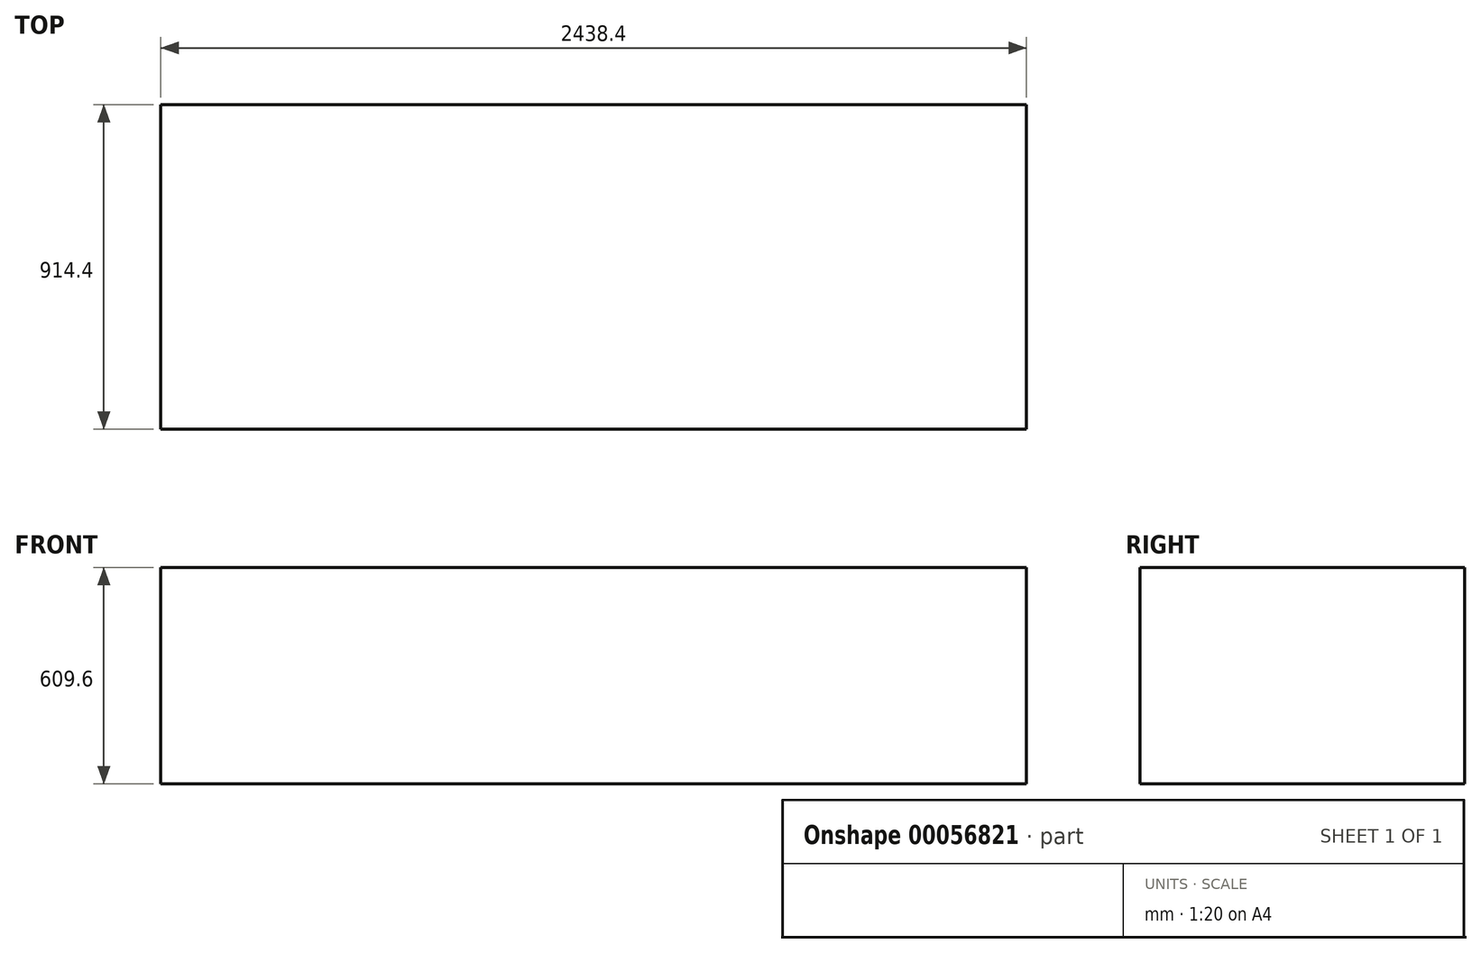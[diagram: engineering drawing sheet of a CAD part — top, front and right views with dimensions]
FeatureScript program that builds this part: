
annotation { "Feature Type Name" : "Feature", "Feature Type Description" : "" }
export const myFeature = defineFeature(function(context is Context, id is Id, definition is map)
    precondition{}
    {
        {
            var Q0;
            Q0=qCreatedBy(makeId("Top.planeOp"),FACE);
            var sketch = newSketch(context, id + "F0", { "sketchPlane" : qUnion([Q0])});
            skLineSegment(sketch, "E0.rect.bottom", {"start": v(1219.2, -457.2) * mm, "end": v(-1219.2, -457.2) * mm});
            skLineSegment(sketch, "E0.rect.top", {"start": v(1219.2, 457.2) * mm, "end": v(-1219.2, 457.2) * mm});
            skLineSegment(sketch, "E0.rect.left", {"start": v(1219.2, -457.2) * mm, "end": v(1219.2, 457.2) * mm});
            skLineSegment(sketch, "E0.rect.right", {"start": v(-1219.2, -457.2) * mm, "end": v(-1219.2, 457.2) * mm});
            skPoint(sketch, "E0.rect.middle", {"position": v(0, 0) * mm});
            skSolve(sketch);
        }
        {
            var Q0;
            Q0=makeQuery(id+"F0.imprint","IMPRINT",FACE,{"disambiguationData":[TD([[makeQuery(id+"F0.imprint","IMPRINT",EDGE,{"derivedFrom":sQuery(id+"F0.wireOp",EDGE,"E0.rect.bottom")}),-1.0]])]});
            extrude(context, id + "F1", {"entities" : qUnion([Q0]), "depth" : 609.6 * mm});
        }
    });
